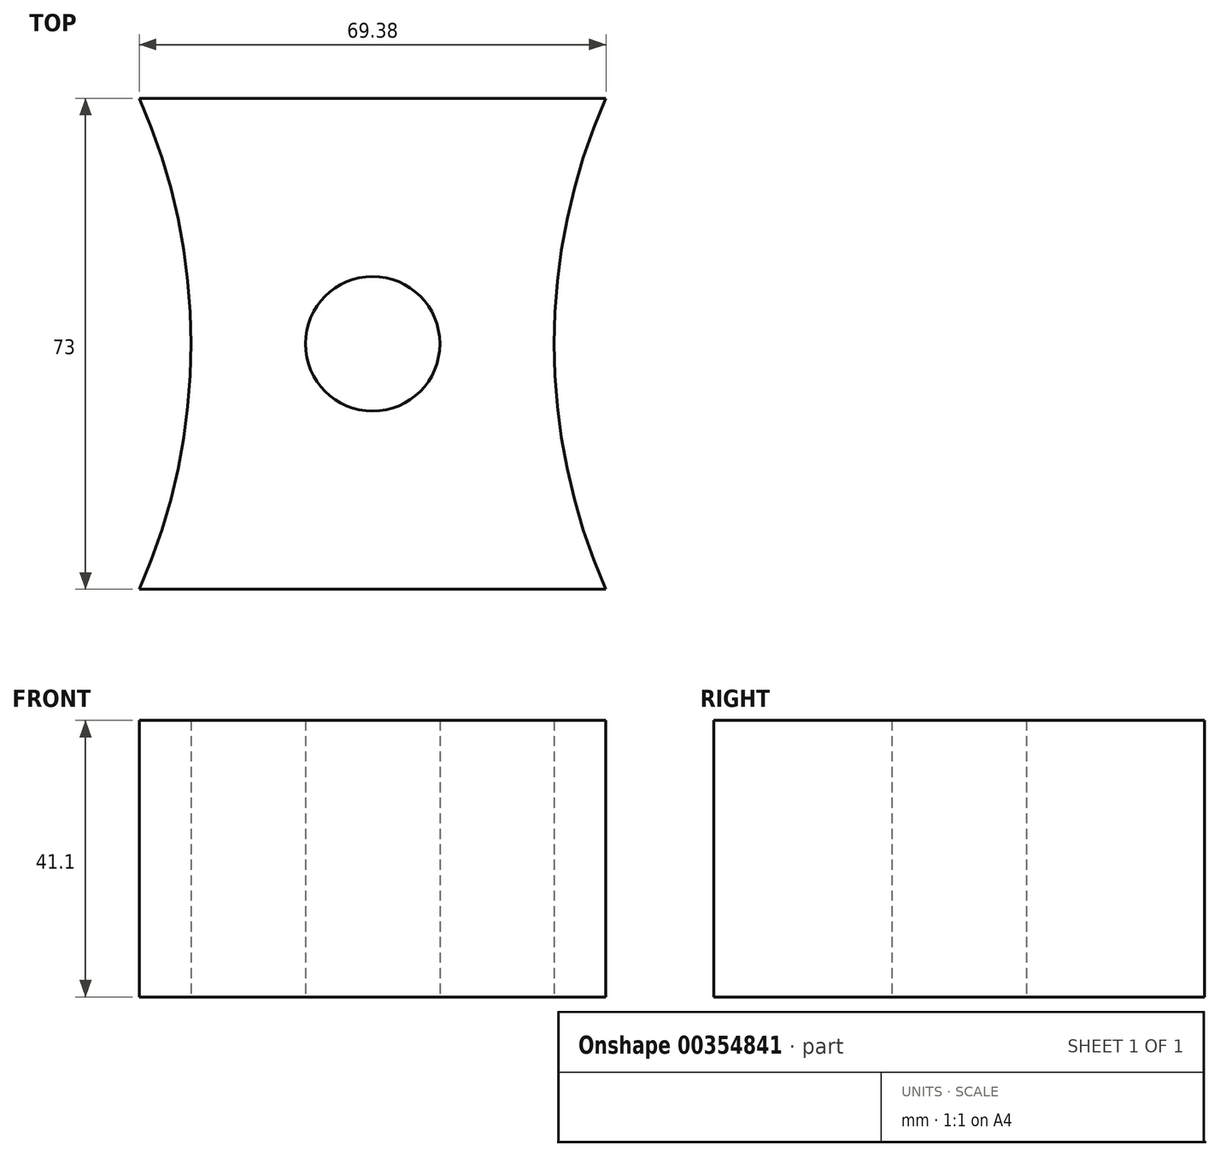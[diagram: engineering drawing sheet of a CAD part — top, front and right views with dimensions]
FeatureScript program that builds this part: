
annotation { "Feature Type Name" : "Feature", "Feature Type Description" : "" }
export const myFeature = defineFeature(function(context is Context, id is Id, definition is map)
    precondition{}
    {
        {
            var Q0;
            Q0=qCreatedBy(makeId("Top.planeOp"),FACE);
            var sketch = newSketch(context, id + "F0", { "sketchPlane" : qUnion([Q0])});
            skArc(sketch, "E0", {"start": v(-34.69, -36.5) * mm, "mid": v(-27, 0) * mm, "end": v(-34.69, 36.5) * mm});
            skArc(sketch, "E1", {"start": v(34.69, 36.5) * mm, "mid": v(27, 0) * mm, "end": v(34.69, -36.5) * mm});
            skLineSegment(sketch, "E2", {"start": v(-34.69, 36.5) * mm, "end": v(34.69, 36.5) * mm});
            skLineSegment(sketch, "E3", {"start": v(-34.69, -36.5) * mm, "end": v(34.69, -36.5) * mm});
            skCircle(sketch, "E4", {"center": v(0, 0) * mm, "radius": 10 * mm});
            skSolve(sketch);
        }
        {
            var Q0;
            Q0=makeQuery(id+"F0.imprint","IMPRINT",FACE,{"disambiguationData":[TD([[makeQuery(id+"F0.imprint","IMPRINT",EDGE,{"derivedFrom":sQuery(id+"F0.wireOp",EDGE,"2QCYRvUC-ctxB-1gh8-ZCTd-1HZbAAyiSap3")}),-1.0]])]});
            var Q1;
            {var subQ0=sQuery(id+"F0.wireOp",EDGE,"E2");Q1=makeQuery(id+"F0.imprint","IMPRINT",FACE,{"disambiguationData":[TD([[makeQuery(id+"F0.imprint","IMPRINT",EDGE,{"derivedFrom":subQ0}),-1.0]])]});}
            var Q2;
            {var subQ0=sQuery(id+"F0.wireOp",EDGE,"E1");var subQ1=makeQuery(id+"F0.imprint","INTERSECT",VERTEX,{"derivedFrom":[subQ0,sQuery(id+"F0.wireOp",EDGE,"E2")]});Q2=makeQuery(id+"F0.imprint","IMPRINT",FACE,{"disambiguationData":[TD([[makeQuery(id+"F0.imprint","IMPRINT",EDGE,{"disambiguationData":[TD([[subQ1,-1.0]])],"derivedFrom":subQ0}),1.0]])]});}
            extrude(context, id + "F1", {"entities" : qUnion([Q0, Q1, Q2]), "depth" : 41.1 * mm});
        }
    });
